# Revit family: 0047800 Feilo Sylvania Lighting Fixtures START WATERPROOF LED 662MM SINGLE 6500K
name_source: partatom
category: Lighting Fixtures
revit_build: Autodesk Revit 2017 (Build: 20190507_1515(x64)
units: mm (PartAtom-declared; Revit-internal decimal feet)

## family parameters
Cut with Voids When Loaded = No
Host = Face
Light Source = Yes
OmniClass Number = 23.80.70.11.17
OmniClass Title = Specialized Lighting by Location or Use
Part Type = Normal
Room Calculation Point = No
Round Connector Dimension = Use Diameter
Shared = No

## types (1)
- START WATERPROOF LED 662MM SINGLE 6500K
    Apparent Load = 12 VA
    Assembly Code = D5020200
    AssetType = Fixed
    Body Material = Polycarbonate_Body_Sylvania_Brite White
    Bracket-Diffuser Material = <By Category>
    Bracket-Mounting Material = <By Category>
    Color Filter = 16777215
    Default Elevation = 0 mm  [stored 0 ft]
    Description = Weather resistant LED Luminaire, 662MM with Single Lamp, 12W at 6500K, 108lm/W. UV stablised polycarbonate cover with specially designed opal lens - softens and control the light whilst optimising output.  No yellow staining. Highly efficient electronic driver included as standard. Smooth body finish, easy to handle. Minimal maintainence with no replacement of lamps . Through wiring achievable. IP65 rating and IK08 body durable for harsh locations. Professionally finished with Stainless Steel brackets. Suspension compatible.
    Diffuser Material = Polycarbonate_Diffuser_Sylvania_Clear
    DiffuserBracketsLength_FEILO = 502 mm
    Dimming Lamp Color Temperature Shift = <None>
    DimmingControlOptions = Non dimmable
    DocumentationLiterature = http://www.sylvania-lighting.com
    DurationUnit = hours
    ElectricShockClassification = Class I
    Emit Shape Visible in Rendering = No
    Emit from Rectangle Length = 642 mm
    Emit from Rectangle Width = 55 mm
    ExpectedLife = 50000
    Height_FEILO = 91 mm  [stored 0.298556 ft]
    IfcExportAs = IfcLightFixtureType
    IfcExportType = IfcLightFixtureType
    ImpactProtectionIndex = IK08
    IngressProtection = IP65
    InputVoltage = 220-240V~
    Keynote = 16500
    Lamp = LED
    Lamp Material = Acrylic High Luminance Glass_Lamp_Sylvania_White
    LampColourRenderingIndex = 0
    LampColourTemperature = 6500 K
    LampNominalLuminous = 1300 lm
    LampSingle_FEILO = Yes
    LampTwin_FEILO = No
    LampsType = LED
    LengthHelp_FEILO = 602 mm
    Length_FEILO = 662 mm
    LightOutputRatio = 100
    LuminousEfficacy = 108.33 lm/W
    Manufacturer = Feilo Sylvania
    ManufacturerName = Feilo Sylvania
    Material = polycarbonate housing, polycarbonate diffuser
    Model = START WATERPROOF LED 1265MM SINGLE 4000K
    ModelNumber = 0047800
    ModelReference = START WATERPROOF LED 662MM SINGLE 6500K
    MountingBracketsLength_FEILO = 390 mm  [stored 1.27953 ft]
    MountingBracketsWidth_FEILO = 41 mm  [stored 0.134514 ft]
    Name = START WATERPROOF LED 662MM SINGLE 6500K
    NominalHeight = 91 mm  [stored 0.298556 ft]
    NominalLength = 662 mm
    NominalWidth = 0 mm  [stored 0 ft]
    NumberOfDiffuserBrackets_FEILO = 3
    Photometric Web File = 0047800.ies
    PowerConsumption = 12 W
    PowerFactor = 0
    SideVoidWidth_FEILO = 45 mm  [stored 0.147638 ft]
    Tilt Angle = -90.00°
    TypeName = START WATERPROOF LED 662MM SINGLE 6500K
    URL = http://www.sylvania-lighting.com
    Voltage = 230 V
    Weight = 0.952 kg
    WidthHelp_FEILO = 15 mm  [stored 0.0492126 ft]
    Width_FEILO = 83 mm

note: [stored X ft] marks values corroborated as IEEE doubles in the binary element streams (Revit-internal decimal feet)

## geometry (parser evidence)
native form markers: Sweep x9
no freeform markers — native parametric forms only
